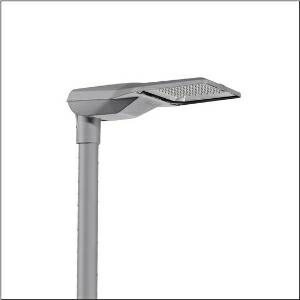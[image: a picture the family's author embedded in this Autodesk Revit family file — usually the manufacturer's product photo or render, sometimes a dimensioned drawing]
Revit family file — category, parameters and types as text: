
# Revit family: streetlight_sl_21_iq_midi___st1_0a_5xe3d61g08nb_ea68
name_source: partatom
category: Lighting Fixtures
units: mm (PartAtom-declared; Revit-internal decimal feet)

## family parameters
Cut with Voids When Loaded = No
Host = Face
Light Source = No
Part Type = Normal
Room Calculation Point = No
Round Connector Dimension = Use Diameter
Shared = No

## types (1)
- --- (1 x LED, 20820 lm, 155.5 W, 2700K)
    Apparent Load = 155 VA
    CIE Flux Codes = 40 73 97 100 100
    Color Rendering = 70
    Color Temperature = 2700K
    Default Elevation = 1800 mm
    Description = Streetlight SL 21 iQ midi, mast luminaire, primary light control with lens, of PMMA, primary optical cover: cover, of toughened safety glass, transparent, light distribution: ST1.0a, light emission: direct distribution, primary light characteristic: asymmetric, installation type: post-top, side-entry, LED, High Power LED, rated luminous flux: 20.820lm, luminous efficacy: 134lm/W, light colour: 727, colour temperature: 2700K, control gear: iQ Street-Remote, control: Street-Remote, Auto-Match, Temp-Guard, Lumen-Switch, Night-Set, Smart-Wire, Light-Fading, Desk-Remote (wireless, voltage-free reading and setting of iQ features in the workshop via application-optimized NFC function/RFID function), optimised constant luminous flux control (CLO 2.0), pre-setting: linear dimming characteristic, mains connection: 230..240V, AC, 50/60Hz, start of lifetime: 156W, end of service life: 162W, reduction: 69W, luminaire housing, of diecast aluminium, powder-coated, SITECO metallic grey (DB 702S), corrosivity category C5 high according to DIN EN ISO 12944, please order mast flange separately, inclination adjustable: 0°, 5°, 10°, 15°, sealing non-destructively replaceable, multi-level sealing system, length: 644mm, width: 335mm, height: 110mm, mast flange for spigot size: 42mm (side-entry): 5XC10008XM4, 60/48mm (side-entry/post-top): 5XC10108XM2, 76/60mm (side-entry/post-top): 5XC10108XM1, mounting height: 4..8m, protection rating (complete): IP66, insulation class (complete): insulation class II (safety insulation), certification: CE, ENEC, ENEC+, VDE, impact resistance: IK10, permissible operating ambient temperature for outdoor applications: -40..+50°C, standard-compliant lighting for roads and squares, packaging unit: 1 piece

Light Distribution: ST1.0a
    Height = 111 mm
    Lamp = 1 x LED
    Lamp Light Flux = 20820 lm
    Lamp Power = 155.5 W
    Lamp count = 1
    Length = 644 mm
    Luminous efficacy = 134 lm/W
    Manufacturer = Siteco
    ModVariant = No
    Model = 5XE3D61G08NB
    Number of Poles = 1
    OnlyDefault = Yes
    Power Factor = 1
    Product Name = Streetlight SL 21 iQ midi | ST1.0a
    Product group = mast luminaire | pylon top
    ProductGroupID = 6100
    Protection Class = Protection class II
    Protection Degree = IP 66
    RLX_Detail_Level = 1
    RLX_Emergency_Light_Flux = 0 lm
    RLX_Emergency_Type = 0
    RLX_Emergency_Type_DB = No
    RlxData = <blob elided: 27217 chars, md5=1c7a24c3>
    Socket = socket
    Standby Power = 0 W
    System Light Flux = 20820 lm
    System Power = 155 W
    Type Comments = factory setting: luminous flux: 100 % | dim-lin: 254 | 823 mA
    Type Image = l_1004298.jpg
    URL = http://relux.com
    VarID = @adj_170167
    Voltage = 0 V
    Weight = 0.00 kg
    Width = 336 mm

## geometry (parser evidence)
native form markers: Blend x4, Sweep x10
no freeform markers — native parametric forms only
